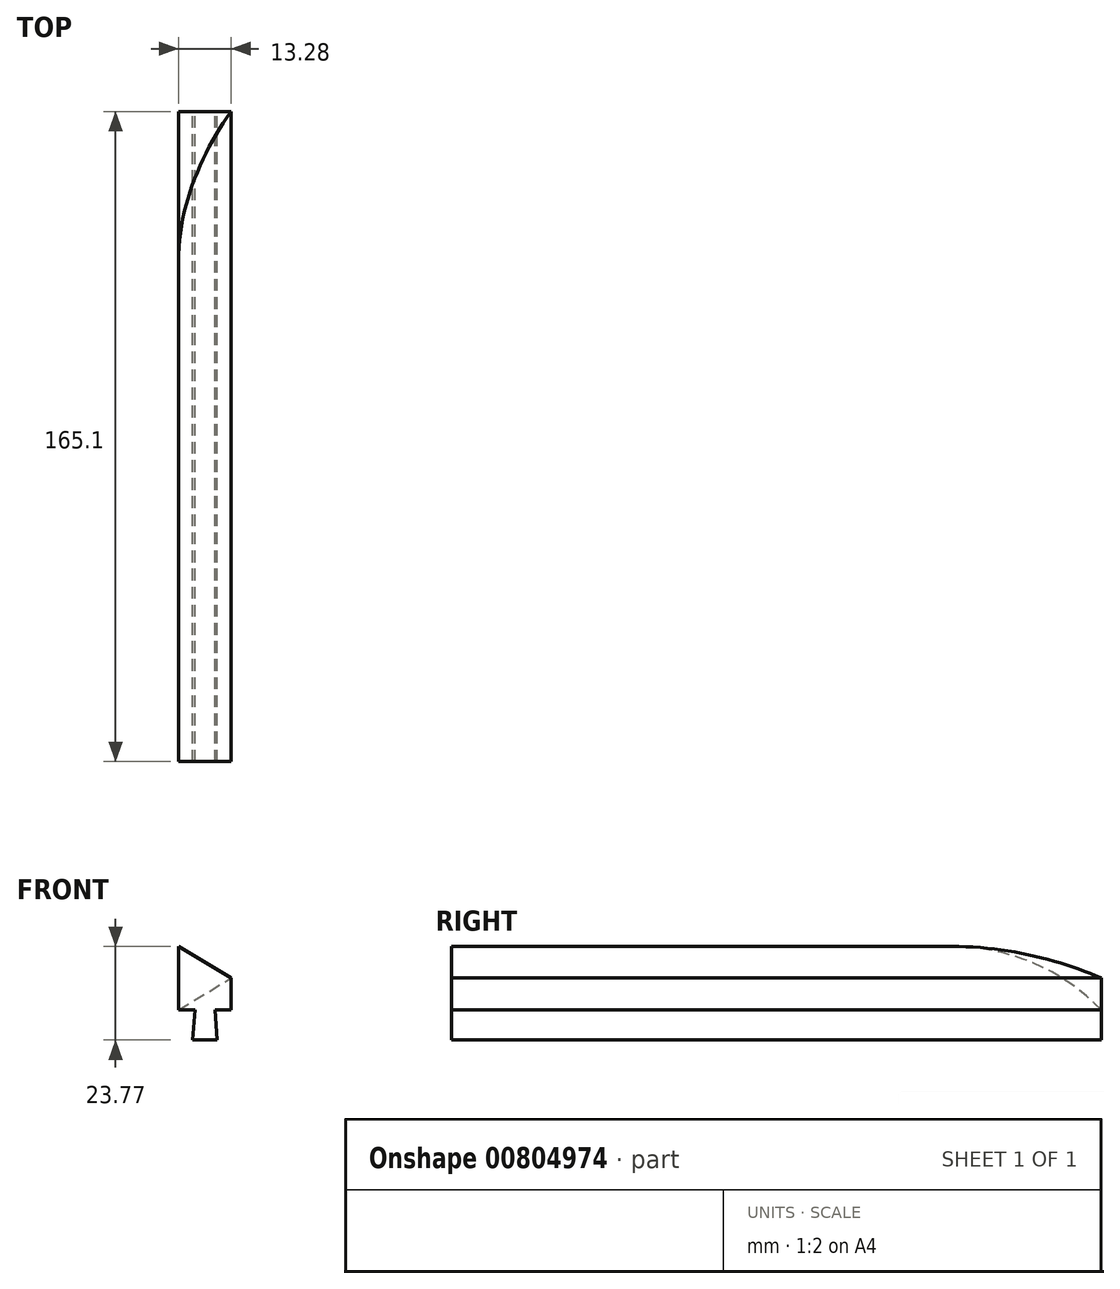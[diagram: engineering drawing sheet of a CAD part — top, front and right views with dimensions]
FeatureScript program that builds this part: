
annotation { "Feature Type Name" : "Feature", "Feature Type Description" : "" }
export const myFeature = defineFeature(function(context is Context, id is Id, definition is map)
    precondition{}
    {
        {
            var Q0;
            Q0=qCreatedBy(makeId("Front.planeOp"),FACE);
            var sketch = newSketch(context, id + "F0", { "sketchPlane" : qUnion([Q0])});
            skLineSegment(sketch, "E0", {"start": v(4.13, 0) * mm, "end": v(0, 0) * mm});
            skLineSegment(sketch, "E1", {"start": v(0, 0) * mm, "end": v(0, 16.15) * mm});
            skLineSegment(sketch, "E2", {"start": v(0, 16.15) * mm, "end": v(13.28, 8.13) * mm});
            skLineSegment(sketch, "E3", {"start": v(13.28, 8.13) * mm, "end": v(13.28, 0) * mm});
            skLineSegment(sketch, "E4", {"start": v(13.28, 0) * mm, "end": v(9.2, 0) * mm});
            skLineSegment(sketch, "E5", {"start": v(4.13, 0) * mm, "end": v(3.53, -7.62) * mm});
            skLineSegment(sketch, "E6", {"start": v(3.53, -7.62) * mm, "end": v(9.75, -7.62) * mm});
            skLineSegment(sketch, "E7", {"start": v(9.75, -7.62) * mm, "end": v(9.2, 0) * mm});
            skPoint(sketch, "E8.orphan", {"position": v(0, 0) * mm});
            skSolve(sketch);
        }
        {
            var Q0;
            Q0=qSketchRegion(id+"F0",true);
            extrude(context, id + "F1", {"entities" : qUnion([Q0]), "depth" : 165.1 * mm, "offsetDistance" : 25.4 * mm});
        }
        {
            var Q0;
            Q0=makeQuery(id+"F1.opExtrude","CAP_FACE",FACE,{"disambiguationData":[OSD([sQuery(id+"F0.wireOp",EDGE,"E0"),sQuery(id+"F0.wireOp",EDGE,"E1"),sQuery(id+"F0.wireOp",EDGE,"E2"),sQuery(id+"F0.wireOp",EDGE,"E3"),sQuery(id+"F0.wireOp",EDGE,"E4"),sQuery(id+"F0.wireOp",EDGE,"E5"),sQuery(id+"F0.wireOp",EDGE,"E6"),sQuery(id+"F0.wireOp",EDGE,"E7")])],"isStart":true});
            var sketch = newSketch(context, id + "F2", { "sketchPlane" : qUnion([Q0])});
            skLineSegment(sketch, "E9", {"start": v(0, 16.15) * mm, "end": v(0, 0) * mm});
            skLineSegment(sketch, "E10", {"start": v(0, 0) * mm, "end": v(-13.28, 8.13) * mm});
            skLineSegment(sketch, "E11", {"start": v(-13.28, 8.13) * mm, "end": v(0, 16.15) * mm});
            skSolve(sketch);
        }
        {
            var Q0;
            Q0=makeQuery(id+"F1.opExtrude","SWEPT_FACE",FACE,{"disambiguationData":[OSD([sQuery(id+"F0.wireOp",EDGE,"E1")])]});
            var sketch = newSketch(context, id + "F3", { "sketchPlane" : qUnion([Q0])});
            skArc(sketch, "E12", {"start": v(38.1, 16.15) * mm, "mid": v(17.4, 11.95) * mm, "end": v(0, 0) * mm});
            skSolve(sketch);
        }
        {
            var Q0;
            Q0=makeQuery(id+"F2.imprint","IMPRINT",FACE,{"disambiguationData":[TD([[makeQuery(id+"F2.imprint","IMPRINT",EDGE,{"derivedFrom":sQuery(id+"F2.wireOp",EDGE,"E9")}),1.0]])]});
            var Q1;
            Q1=sQuery(id+"F3.wireOp",EDGE,"E12");
            sweep(context, id + "F4", {"operationType" : NewBodyOperationType.REMOVE, "profiles" : qUnion([Q0]), "path" : qUnion([Q1])});
        }
    });
